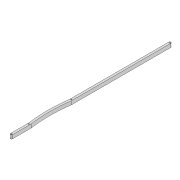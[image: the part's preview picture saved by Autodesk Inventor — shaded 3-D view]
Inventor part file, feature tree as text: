
AUTODESK INVENTOR PART (.ipt)
format: ipt  version: 2022 (Build 260153000, 153)  size: 123,392 bytes
history: native  units: mm
features: extrude x2, sketch x2, projected_geometry x1
ambient origin geometry x8: Origin, YZ Plane, XZ Plane, XY Plane, X Axis, Y Axis, Z Axis, Center Point
bodies: Solid1 (feature_tree)
feature tree (5):
  extrude  "Extrusion1"  Depth=441.93mm
  extrude  "Extrusion2"  Depth=3.0mm
  sketch  "Sketch1"  dims[d0=6.0mm d1=441.93mm]
  sketch  "Sketch2"  dims[d2=3.0mm d3=3.0mm d4=10.0mm d5=0.0mm d20=3.0mm d21=48.203mm d22=3.0mm d23=166.766mm d24=400.0mm d25=400.0mm d26=3.0mm d28=3.0mm d29=4.363323mm d30=4.363323mm d31=100.0mm d32=0.0mm]
  projected_geometry  "Projected Loop1"
